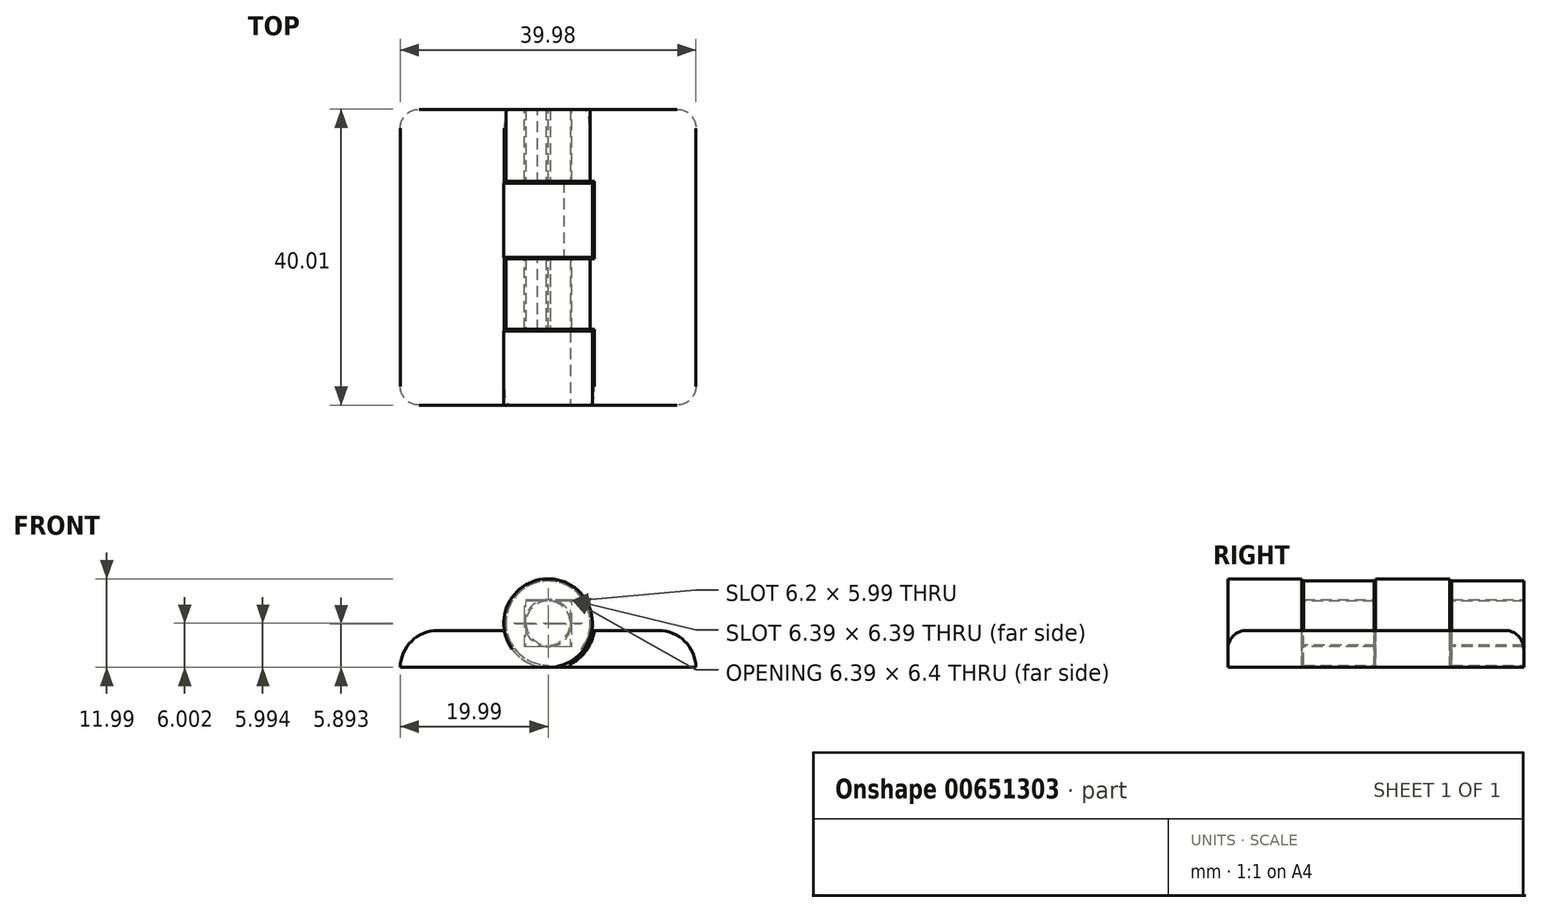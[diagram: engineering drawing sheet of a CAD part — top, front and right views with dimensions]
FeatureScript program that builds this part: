
annotation { "Feature Type Name" : "Feature", "Feature Type Description" : "" }
export const myFeature = defineFeature(function(context is Context, id is Id, definition is map)
    precondition{}
    {
        {
            var Q0;
            Q0=qCreatedBy(makeId("Front.planeOp"),FACE);
            var sketch = newSketch(context, id + "F0", { "sketchPlane" : qUnion([Q0])});
            skLineSegment(sketch, "E0", {"start": v(0, 0) * mm, "end": v(-19.99, 0) * mm});
            skLineSegment(sketch, "E1", {"start": v(-19.99, 0) * mm, "end": v(-19.99, 5) * mm});
            skLineSegment(sketch, "E2", {"start": v(-19.99, 5) * mm, "end": v(-5.91, 5) * mm});
            skCircle(sketch, "E3", {"center": v(0, 6) * mm, "radius": 6 * mm});
            skPoint(sketch, "E4.start.orphan", {"position": v(0, 5) * mm});
            skArc(sketch, "E5.0", {"start": v(2.1, 0) * mm, "mid": v(4.87, 1.93) * mm, "end": v(6.27, 5) * mm});
            skLineSegment(sketch, "E6", {"start": v(0, 0) * mm, "end": v(2.1, 0) * mm});
            skLineSegment(sketch, "E7", {"start": v(2.1, 0) * mm, "end": v(19.99, 0) * mm});
            skLineSegment(sketch, "E8", {"start": v(19.99, 0) * mm, "end": v(19.99, 5) * mm});
            skLineSegment(sketch, "E9", {"start": v(19.99, 5) * mm, "end": v(6.27, 5) * mm});
            skLineSegment(sketch, "E10", {"start": v(6.27, 5) * mm, "end": v(5.91, 5) * mm});
            skArc(sketch, "E11", {"start": v(0.3, 3.01) * mm, "mid": v(0, 9) * mm, "end": v(-0.3, 3.01) * mm});
            skLineSegment(sketch, "E12", {"start": v(0.3, 3.01) * mm, "end": v(0.3, 2.8) * mm});
            skLineSegment(sketch, "E13", {"start": v(-0.3, 3.01) * mm, "end": v(-0.3, 2.8) * mm});
            skArc(sketch, "E14", {"start": v(-0.3, 2.8) * mm, "mid": v(0, 2.8) * mm, "end": v(0.3, 2.8) * mm});
            skSolve(sketch);
        }
        {
            var Q0;
            Q0=qCreatedBy(makeId("Front.planeOp"),FACE);
            cPlane(context, id + "F1", {"entities" : qUnion([Q0]), "cplaneType" : CPlaneType.OFFSET, "offset" : 40 * mm, "oppositeDirection" : true, "width" : 152.4 * mm, "height" : 152.4 * mm});
        }
        {
            var Q0;
            Q0=qCreatedBy(id+"F1.planeOp",FACE);
            var sketch = newSketch(context, id + "F2", { "sketchPlane" : qUnion([Q0])});
            skArc(sketch, "E15", {"start": v(-5.91, 5) * mm, "mid": v(-4.42, 1.95) * mm, "end": v(-1.51, 0.2) * mm});
            skLineSegment(sketch, "E16", {"start": v(0, 0) * mm, "end": v(19.99, 0) * mm});
            skLineSegment(sketch, "E17", {"start": v(19.99, 0) * mm, "end": v(19.99, 5) * mm});
            skArc(sketch, "E18", {"start": v(5.6, 5) * mm, "mid": v(-3.66, 10.35) * mm, "end": v(0, 0.3) * mm});
            skLineSegment(sketch, "E19", {"start": v(19.99, 5) * mm, "end": v(5.6, 5) * mm});
            skLineSegment(sketch, "E20", {"start": v(-1.54, 0) * mm, "end": v(-19.99, 0) * mm});
            skLineSegment(sketch, "E21", {"start": v(-19.99, 0) * mm, "end": v(-19.99, 5) * mm});
            skLineSegment(sketch, "E22", {"start": v(-19.99, 5) * mm, "end": v(-5.91, 5) * mm});
            skLineSegment(sketch, "E23", {"start": v(0, 0) * mm, "end": v(0, 0.3) * mm});
            skArc(sketch, "E24.trimOffspring", {"start": v(0, 0) * mm, "mid": v(3.87, 1.42) * mm, "end": v(5.91, 5) * mm});
            skArc(sketch, "E25", {"start": v(-1.54, 0) * mm, "mid": v(-1.44, 0.09) * mm, "end": v(-1.51, 0.2) * mm});
            skCircle(sketch, "E26", {"center": v(0, 6) * mm, "radius": 3.2 * mm});
            skSolve(sketch);
        }
        {
            var Q0;
            Q0=makeQuery(id+"F0.imprint","IMPRINT",FACE,{"disambiguationData":[TD([[makeQuery(id+"F0.imprint","IMPRINT",EDGE,{"derivedFrom":sQuery(id+"F0.wireOp",EDGE,"E11")}),-1.0]])]});
            var Q1;
            {var subQ0=sQuery(id+"F0.wireOp",EDGE,"E0");Q1=makeQuery(id+"F0.imprint","IMPRINT",FACE,{"disambiguationData":[TD([[makeQuery(id+"F0.imprint","IMPRINT",EDGE,{"derivedFrom":subQ0}),-1.0]])]});}
            extrude(context, id + "F3", {"entities" : qUnion([Q0, Q1]), "oppositeDirection" : true, "depth" : 10 * mm, "offsetDistance" : 25.4 * mm});
        }
        {
            var Q0;
            Q0=makeQuery(id+"F0.imprint","IMPRINT",FACE,{"disambiguationData":[TD([[makeQuery(id+"F0.imprint","IMPRINT",EDGE,{"derivedFrom":sQuery(id+"F0.wireOp",EDGE,"E11")}),1.0]])]});
            extrude(context, id + "F4", {"entities" : qUnion([Q0]), "operationType" : NewBodyOperationType.ADD, "oppositeDirection" : true, "depth" : 40 * mm, "offsetDistance" : 25.4 * mm});
        }
        {
            var Q0;
            Q0=qCreatedBy(id+"F1.planeOp",FACE);
            cPlane(context, id + "F5", {"entities" : qUnion([Q0]), "cplaneType" : CPlaneType.OFFSET, "offset" : 10 * mm, "width" : 152.4 * mm, "height" : 152.4 * mm});
        }
        {
            var Q0;
            Q0=makeQuery(id+"F0.imprint","IMPRINT",FACE,{"disambiguationData":[TD([[makeQuery(id+"F0.imprint","IMPRINT",EDGE,{"derivedFrom":sQuery(id+"F0.wireOp",EDGE,"E11")}),-1.0]])]});
            var Q1;
            {var subQ0=sQuery(id+"F0.wireOp",EDGE,"E0");Q1=makeQuery(id+"F0.imprint","IMPRINT",FACE,{"disambiguationData":[TD([[makeQuery(id+"F0.imprint","IMPRINT",EDGE,{"derivedFrom":subQ0}),-1.0]])]});}
            var Q2;
            Q2=qCreatedBy(id+"F5.planeOp",FACE);
            extrude(context, id + "F6", {"entities" : qUnion([Q0, Q1]), "operationType" : NewBodyOperationType.ADD, "endBound" : BoundingType.UP_TO_SURFACE, "oppositeDirection" : true, "depth" : 29.46 * mm, "endBoundEntityFace" : qUnion([Q2]), "offsetDistance" : 25.4 * mm, "hasSecondDirection" : true, "secondDirectionOppositeDirection" : true, "secondDirectionDepth" : 19.99 * mm});
        }
        {
            var Q0;
            Q0=makeQuery(id+"F2.imprint","IMPRINT",FACE,{"disambiguationData":[TD([[makeQuery(id+"F2.imprint","IMPRINT",EDGE,{"derivedFrom":sQuery(id+"F2.wireOp",EDGE,"E15")}),-1.0]])]});
            extrude(context, id + "F7", {"entities" : qUnion([Q0]), "operationType" : NewBodyOperationType.ADD, "depth" : 10 * mm, "offsetDistance" : 25.4 * mm});
        }
        {
            var Q0;
            Q0=makeQuery(id+"F3.opExtrude","CAP_FACE",FACE,{"disambiguationData":[OSD([sQuery(id+"F0.wireOp",EDGE,"E0"),sQuery(id+"F0.wireOp",EDGE,"E1"),sQuery(id+"F0.wireOp",EDGE,"E2"),sQuery(id+"F0.wireOp",EDGE,"E3"),sQuery(id+"F0.wireOp",EDGE,"E11"),sQuery(id+"F0.wireOp",EDGE,"E12"),sQuery(id+"F0.wireOp",EDGE,"E13"),sQuery(id+"F0.wireOp",EDGE,"E14")])],"isStart":false});
            cPlane(context, id + "F8", {"entities" : qUnion([Q0]), "cplaneType" : CPlaneType.OFFSET, "offset" : 0.25 * mm, "width" : 152.4 * mm, "height" : 152.4 * mm});
        }
        {
            var Q0;
            {var subQ2=sQuery(id+"F2.wireOp",EDGE,"E18");Q0=makeQuery(id+"F2.imprint","IMPRINT",FACE,{"disambiguationData":[TD([[makeQuery(id+"F2.imprint","IMPRINT",EDGE,{"derivedFrom":subQ2}),1.0]])]});}
            var Q1;
            Q1=makeQuery(id+"F2.imprint","IMPRINT",FACE,{"disambiguationData":[TD([[makeQuery(id+"F2.imprint","IMPRINT",EDGE,{"derivedFrom":sQuery(id+"F2.wireOp",EDGE,"E16")}),1.0]])]});
            var Q2;
            Q2=qCreatedBy(id+"F8.planeOp",FACE);
            extrude(context, id + "F9", {"entities" : qUnion([Q0, Q1]), "operationType" : NewBodyOperationType.ADD, "endBound" : BoundingType.UP_TO_SURFACE, "depth" : 25.4 * mm, "endBoundEntityFace" : qUnion([Q2]), "offsetDistance" : 25.4 * mm, "hasSecondDirection" : true, "secondDirectionOppositeDirection" : false, "secondDirectionDepth" : 20.24 * mm});
        }
        {
            var Q0;
            Q0=makeQuery(id+"F0.imprint","IMPRINT",FACE,{"disambiguationData":[TD([[makeQuery(id+"F0.imprint","IMPRINT",EDGE,{"derivedFrom":sQuery(id+"F0.wireOp",EDGE,"E5.0")}),-1.0]])]});
            extrude(context, id + "F10", {"entities" : qUnion([Q0]), "operationType" : NewBodyOperationType.ADD, "oppositeDirection" : true, "depth" : 10.26 * mm, "offsetDistance" : 25.4 * mm});
        }
        {
            var Q0;
            Q0=makeQuery(id+"F2.imprint","IMPRINT",FACE,{"disambiguationData":[TD([[makeQuery(id+"F2.imprint","IMPRINT",EDGE,{"derivedFrom":sQuery(id+"F2.wireOp",EDGE,"E15")}),-1.0]])]});
            var Q1;
            Q1=makeQuery(id+"F3.opExtrude","CAP_FACE",FACE,{"disambiguationData":[OSD([sQuery(id+"F0.wireOp",EDGE,"E0"),sQuery(id+"F0.wireOp",EDGE,"E1"),sQuery(id+"F0.wireOp",EDGE,"E2"),sQuery(id+"F0.wireOp",EDGE,"E3"),sQuery(id+"F0.wireOp",EDGE,"E11"),sQuery(id+"F0.wireOp",EDGE,"E12"),sQuery(id+"F0.wireOp",EDGE,"E13"),sQuery(id+"F0.wireOp",EDGE,"E14")])],"isStart":false});
            var Q2;
            Q2=makeQuery(id+"F6.opExtrude","CAP_FACE",FACE,{"disambiguationData":[OSD([sQuery(id+"F0.wireOp",EDGE,"E0"),sQuery(id+"F0.wireOp",EDGE,"E1"),sQuery(id+"F0.wireOp",EDGE,"E2"),sQuery(id+"F0.wireOp",EDGE,"E3"),sQuery(id+"F0.wireOp",EDGE,"E11"),sQuery(id+"F0.wireOp",EDGE,"E12"),sQuery(id+"F0.wireOp",EDGE,"E13"),sQuery(id+"F0.wireOp",EDGE,"E14")])],"isStart":true});
            extrude(context, id + "F11", {"entities" : qUnion([Q0]), "operationType" : NewBodyOperationType.ADD, "endBound" : BoundingType.UP_TO_SURFACE, "depth" : 25.4 * mm, "endBoundEntityFace" : qUnion([Q1]), "offsetDistance" : 25.4 * mm, "hasSecondDirection" : true, "secondDirectionBound" : BoundingType.UP_TO_SURFACE, "secondDirectionOppositeDirection" : false, "secondDirectionDepth" : 28.45 * mm, "secondDirectionBoundEntityFace" : qUnion([Q2])});
        }
        {
            var Q0;
            Q0=makeQuery(id+"F0.imprint","IMPRINT",FACE,{"disambiguationData":[TD([[makeQuery(id+"F0.imprint","IMPRINT",EDGE,{"derivedFrom":sQuery(id+"F0.wireOp",EDGE,"E5.0")}),-1.0]])]});
            var Q1;
            Q1=makeQuery(id+"F13.opExtrude","CAP_FACE",FACE,{"disambiguationData":[OSD([sQuery(id+"F2.wireOp",EDGE,"E16"),sQuery(id+"F2.wireOp",EDGE,"E17"),sQuery(id+"F2.wireOp",EDGE,"E18"),sQuery(id+"F2.wireOp",EDGE,"E19"),sQuery(id+"F2.wireOp",EDGE,"E23"),sQuery(id+"F2.wireOp",EDGE,"E26")])],"isStart":false});
            var Q2;
            Q2=makeQuery(id+"F9.opExtrude","CAP_FACE",FACE,{"disambiguationData":[OSD([sQuery(id+"F2.wireOp",EDGE,"E16"),sQuery(id+"F2.wireOp",EDGE,"E17"),sQuery(id+"F2.wireOp",EDGE,"E18"),sQuery(id+"F2.wireOp",EDGE,"E19"),sQuery(id+"F2.wireOp",EDGE,"E23"),sQuery(id+"F2.wireOp",EDGE,"E26")])],"isStart":true});
            extrude(context, id + "F12", {"entities" : qUnion([Q0]), "operationType" : NewBodyOperationType.ADD, "oppositeDirection" : true, "depth" : 31.37 * mm, "endBoundEntityFace" : qUnion([Q1]), "offsetDistance" : 25.4 * mm, "hasSecondDirection" : true, "secondDirectionBound" : BoundingType.UP_TO_SURFACE, "secondDirectionOppositeDirection" : true, "secondDirectionDepth" : 26.92 * mm, "secondDirectionBoundEntityFace" : qUnion([Q2])});
        }
        {
            var Q0;
            Q0=makeQuery(id+"F2.imprint","IMPRINT",FACE,{"disambiguationData":[TD([[makeQuery(id+"F2.imprint","IMPRINT",EDGE,{"derivedFrom":sQuery(id+"F2.wireOp",EDGE,"E16")}),1.0]])]});
            var Q1;
            {var subQ2=sQuery(id+"F2.wireOp",EDGE,"E18");Q1=makeQuery(id+"F2.imprint","IMPRINT",FACE,{"disambiguationData":[TD([[makeQuery(id+"F2.imprint","IMPRINT",EDGE,{"derivedFrom":subQ2}),1.0]])]});}
            extrude(context, id + "F13", {"entities" : qUnion([Q0, Q1]), "operationType" : NewBodyOperationType.ADD, "depth" : 9.75 * mm, "offsetDistance" : 25.4 * mm});
        }
        {
            var Q0;
            Q0=makeQuery(id+"F12.opExtrude","TWEAK_EDGE",EDGE,{"derivedFrom":[makeQuery(id+"F0.imprint","IMPRINT",EDGE,{"derivedFrom":sQuery(id+"F0.wireOp",EDGE,"E5.0")}),makeQuery(id+"F0.imprint","IMPRINT",EDGE,{"derivedFrom":sQuery(id+"F0.wireOp",EDGE,"E7")})]});
            var Q1;
            Q1=makeQuery(id+"F10.opExtrude","SWEPT_EDGE",EDGE,{"disambiguationData":[OSD([sQuery(id+"F0.wireOp",EDGE,"E5.0"),sQuery(id+"F0.wireOp",EDGE,"E6"),sQuery(id+"F0.wireOp",EDGE,"E7")])]});
            fillet(context, id + "F14", {"entities" : qUnion([Q0, Q1]), "radius" : 0.25 * mm, "tangentPropagation" : true, "allowEdgeOverflow" : false});
        }
        {
            var Q0;
            Q0=makeQuery(id+"F7.opExtrude","SWEPT_EDGE",EDGE,{"disambiguationData":[OSD([sQuery(id+"F2.wireOp",EDGE,"E21"),sQuery(id+"F2.wireOp",EDGE,"E22")])]});
            var Q1;
            Q1=makeQuery(id+"F6.opExtrude","SWEPT_EDGE",EDGE,{"disambiguationData":[OSD([sQuery(id+"F0.wireOp",EDGE,"E1"),sQuery(id+"F0.wireOp",EDGE,"E2")])]});
            var Q2;
            Q2=makeQuery(id+"F11.opExtrude","TWEAK_EDGE",EDGE,{"derivedFrom":[makeQuery(id+"F2.imprint","IMPRINT",EDGE,{"derivedFrom":sQuery(id+"F2.wireOp",EDGE,"E21")}),makeQuery(id+"F2.imprint","IMPRINT",EDGE,{"derivedFrom":sQuery(id+"F2.wireOp",EDGE,"E22")})]});
            var Q3;
            Q3=makeQuery(id+"F3.opExtrude","SWEPT_EDGE",EDGE,{"disambiguationData":[OSD([sQuery(id+"F0.wireOp",EDGE,"E1"),sQuery(id+"F0.wireOp",EDGE,"E2")])]});
            var Q4;
            Q4=makeQuery(id+"F13.opExtrude","SWEPT_EDGE",EDGE,{"disambiguationData":[OSD([sQuery(id+"F2.wireOp",EDGE,"E17"),sQuery(id+"F2.wireOp",EDGE,"E19")])]});
            var Q5;
            Q5=makeQuery(id+"F12.boolean.opBoolean","MERGE",EDGE,{"derivedFrom":[makeQuery(id+"F9.opExtrude","SWEPT_EDGE",EDGE,{"disambiguationData":[OSD([sQuery(id+"F2.wireOp",EDGE,"E17"),sQuery(id+"F2.wireOp",EDGE,"E19")])]}),makeQuery(id+"F12.opExtrude","TWEAK_EDGE",EDGE,{"derivedFrom":[makeQuery(id+"F0.imprint","IMPRINT",EDGE,{"derivedFrom":sQuery(id+"F0.wireOp",EDGE,"E8")}),makeQuery(id+"F0.imprint","IMPRINT",EDGE,{"derivedFrom":sQuery(id+"F0.wireOp",EDGE,"E9")})]})]});
            var Q6;
            Q6=makeQuery(id+"F10.opExtrude","SWEPT_EDGE",EDGE,{"disambiguationData":[OSD([sQuery(id+"F0.wireOp",EDGE,"E8"),sQuery(id+"F0.wireOp",EDGE,"E9")])]});
            fillet(context, id + "F15", {"entities" : qUnion([Q0, Q1, Q2, Q3, Q4, Q5, Q6]), "radius" : 5.08 * mm, "tangentPropagation" : true, "allowEdgeOverflow" : false});
        }
        {
            var Q0;
            Q0=makeQuery(id+"F13.opExtrude","CAP_EDGE",EDGE,{"disambiguationData":[OSD([sQuery(id+"F2.wireOp",EDGE,"E19")])],"isStart":true});
            var Q1;
            Q1=makeQuery(id+"F7.opExtrude","CAP_EDGE",EDGE,{"disambiguationData":[OSD([sQuery(id+"F2.wireOp",EDGE,"E22")])],"isStart":true});
            var Q2;
            Q2=makeQuery(id+"F3.opExtrude","CAP_EDGE",EDGE,{"disambiguationData":[OSD([sQuery(id+"F0.wireOp",EDGE,"E2")])],"isStart":true});
            var Q3;
            Q3=makeQuery(id+"F10.opExtrude","CAP_EDGE",EDGE,{"disambiguationData":[OSD([sQuery(id+"F0.wireOp",EDGE,"E9")])],"isStart":true});
            fillet(context, id + "F16", {"entities" : qUnion([Q0, Q1, Q2, Q3]), "radius" : 2.54 * mm, "tangentPropagation" : true, "allowEdgeOverflow" : false});
        }
    });
